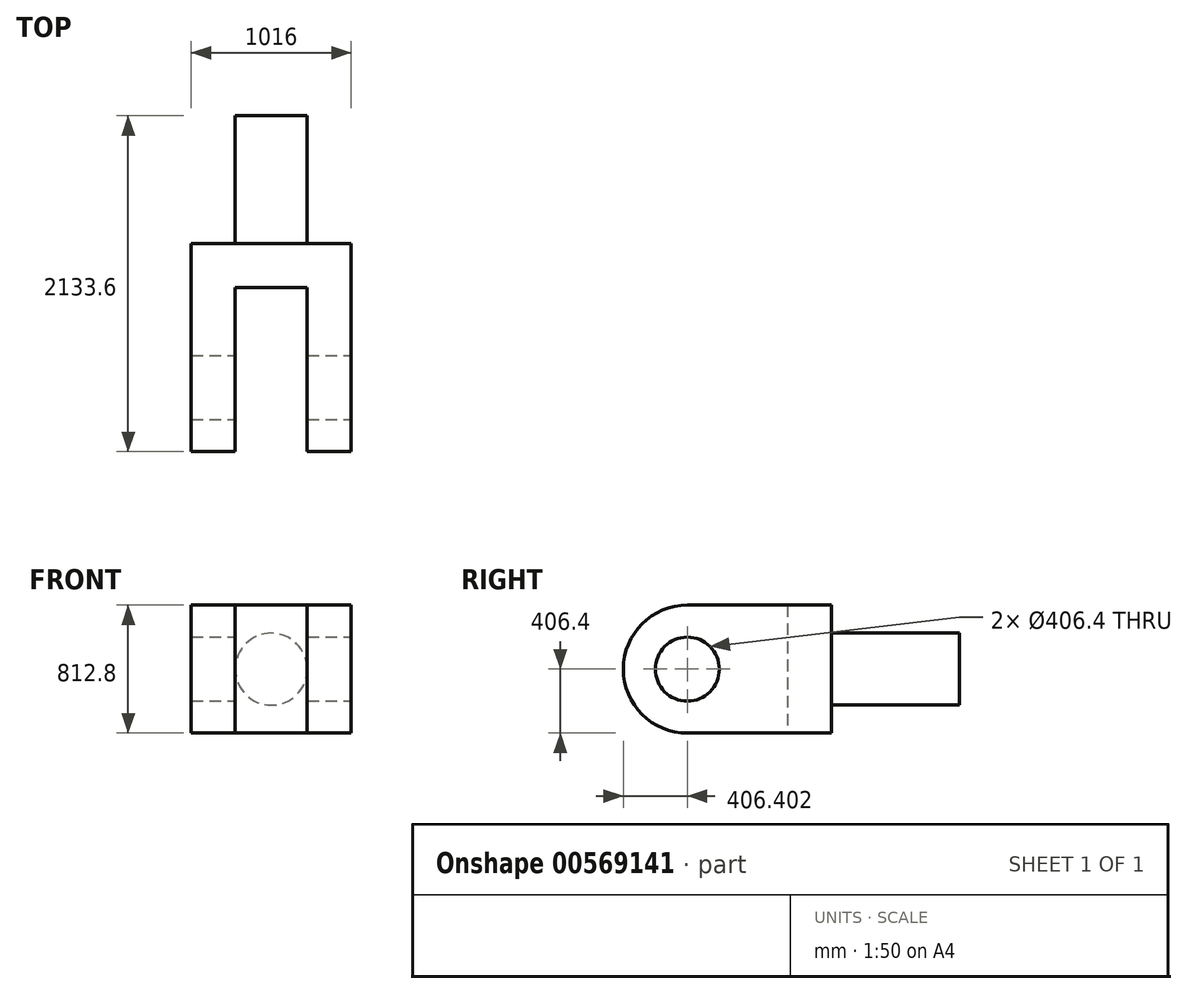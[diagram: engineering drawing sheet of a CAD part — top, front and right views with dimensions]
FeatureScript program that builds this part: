
annotation { "Feature Type Name" : "Feature", "Feature Type Description" : "" }
export const myFeature = defineFeature(function(context is Context, id is Id, definition is map)
    precondition{}
    {
        {
            var Q0;
            Q0=qCreatedBy(makeId("Top.planeOp"),FACE);
            var sketch = newSketch(context, id + "F0", { "sketchPlane" : qUnion([Q0])});
            skLineSegment(sketch, "E0", {"start": v(0, -58.26) * mm, "end": v(279.4, -58.26) * mm});
            skLineSegment(sketch, "E1", {"start": v(279.4, -58.26) * mm, "end": v(279.4, 1262.54) * mm});
            skLineSegment(sketch, "E2", {"start": v(279.4, 1262.54) * mm, "end": v(-736.6, 1262.54) * mm});
            skLineSegment(sketch, "E3", {"start": v(-736.6, 1262.54) * mm, "end": v(-736.6, -58.26) * mm});
            skLineSegment(sketch, "E4", {"start": v(-736.6, -58.26) * mm, "end": v(-457.2, -58.26) * mm});
            skLineSegment(sketch, "E5", {"start": v(-457.2, -58.26) * mm, "end": v(-457.2, 983.14) * mm});
            skLineSegment(sketch, "E6", {"start": v(-457.2, 983.14) * mm, "end": v(0, 983.14) * mm});
            skLineSegment(sketch, "E7", {"start": v(0, 983.14) * mm, "end": v(0, -58.26) * mm});
            skSolve(sketch);
        }
        {
            var Q0;
            Q0=makeQuery(id+"F0.imprint","IMPRINT",FACE,{"disambiguationData":[TD([[makeQuery(id+"F0.imprint","IMPRINT",EDGE,{"derivedFrom":sQuery(id+"F0.wireOp",EDGE,"E0")}),1.0]])]});
            extrude(context, id + "F1", {"entities" : qUnion([Q0]), "depth" : 812.8 * mm, "offsetDistance" : 25.4 * mm});
        }
        {
            var Q0;
            Q0=makeQuery(id+"F1.opExtrude","CAP_FACE",FACE,{"disambiguationData":[OSD([sQuery(id+"F0.wireOp",EDGE,"E0"),sQuery(id+"F0.wireOp",EDGE,"E1"),sQuery(id+"F0.wireOp",EDGE,"E2"),sQuery(id+"F0.wireOp",EDGE,"E3"),sQuery(id+"F0.wireOp",EDGE,"E4"),sQuery(id+"F0.wireOp",EDGE,"E5"),sQuery(id+"F0.wireOp",EDGE,"E6"),sQuery(id+"F0.wireOp",EDGE,"E7")])],"isStart":false});
            var sketch = newSketch(context, id + "F2", { "sketchPlane" : qUnion([Q0])});
            skLineSegment(sketch, "E8", {"start": v(-457.2, 1262.54) * mm, "end": v(-457.2, 2075.34) * mm});
            skLineSegment(sketch, "E9", {"start": v(-457.2, 2075.34) * mm, "end": v(0, 2075.34) * mm});
            skLineSegment(sketch, "E10", {"start": v(0, 2075.34) * mm, "end": v(0, 1262.54) * mm});
            skSolve(sketch);
        }
        {
            var Q0;
            {var subQ0=sQuery(id+"F2.wireOp",EDGE,"E8");Q0=makeQuery(id+"F2.imprint","IMPRINT",FACE,{"disambiguationData":[TD([[makeQuery(id+"F2.imprint","IMPRINT",EDGE,{"derivedFrom":subQ0}),-1.0]])]});}
            extrude(context, id + "F3", {"entities" : qUnion([Q0]), "operationType" : NewBodyOperationType.ADD, "oppositeDirection" : true, "depth" : 812.8 * mm, "offsetDistance" : 25.4 * mm});
        }
        {
            var Q0;
            Q0=makeQuery(id+"F1.opExtrude","CAP_EDGE",EDGE,{"disambiguationData":[OSD([sQuery(id+"F0.wireOp",EDGE,"E0")])],"isStart":false});
            var Q1;
            Q1=makeQuery(id+"F1.opExtrude","CAP_EDGE",EDGE,{"disambiguationData":[OSD([sQuery(id+"F0.wireOp",EDGE,"E4")])],"isStart":false});
            fillet(context, id + "F4", {"entities" : qUnion([Q0, Q1]), "radius" : 406.4 * mm, "tangentPropagation" : true, "allowEdgeOverflow" : false});
        }
        {
            var Q0;
            Q0=makeQuery(id+"F3.opExtrude","SWEPT_FACE",FACE,{"disambiguationData":[OSD([sQuery(id+"F2.wireOp",EDGE,"E9")])]});
            var sketch = newSketch(context, id + "F5", { "sketchPlane" : qUnion([Q0])});
            skCircle(sketch, "E11", {"center": v(228.6, 406.4) * mm, "radius": 228.6 * mm});
            skPoint(sketch, "E11.centerSnap0", {"position": v(457.2, 406.4) * mm});
            skPoint(sketch, "E11.centerSnap1", {"position": v(228.6, 812.8) * mm});
            skSolve(sketch);
        }
        {
            var Q0;
            {var subQ1=sQuery(id+"F2.wireOp",EDGE,"E9");var subQ6=makeQuery(id+"F3.opExtrude","CAP_EDGE",EDGE,{"disambiguationData":[OSD([subQ1])],"isStart":true});Q0=makeQuery(id+"F5.imprint","IMPRINT",FACE,{"disambiguationData":[TD([[makeQuery(id+"F5.imprint","IMPRINT",EDGE,{"derivedFrom":subQ6}),1.0]])]});}
            var Q1;
            {var subQ1=sQuery(id+"F2.wireOp",EDGE,"E9");var subQ6=makeQuery(id+"F3.opExtrude","CAP_EDGE",EDGE,{"disambiguationData":[OSD([subQ1])],"isStart":false});Q1=makeQuery(id+"F5.imprint","IMPRINT",FACE,{"disambiguationData":[TD([[makeQuery(id+"F5.imprint","IMPRINT",EDGE,{"derivedFrom":subQ6}),-1.0]])]});}
            extrude(context, id + "F6", {"entities" : qUnion([Q0, Q1]), "operationType" : NewBodyOperationType.REMOVE, "oppositeDirection" : true, "depth" : 812.8 * mm, "offsetDistance" : 25.4 * mm});
        }
        {
            var Q0;
            Q0=makeQuery(id+"F1.opExtrude","CAP_EDGE",EDGE,{"disambiguationData":[OSD([sQuery(id+"F0.wireOp",EDGE,"E0")])],"isStart":true});
            var Q1;
            Q1=makeQuery(id+"F1.opExtrude","CAP_EDGE",EDGE,{"disambiguationData":[OSD([sQuery(id+"F0.wireOp",EDGE,"E4")])],"isStart":true});
            fillet(context, id + "F7", {"entities" : qUnion([Q0, Q1]), "radius" : 406.4 * mm, "tangentPropagation" : true, "allowEdgeOverflow" : false});
        }
        {
            var Q0;
            Q0=makeQuery(id+"F1.opExtrude","SWEPT_FACE",FACE,{"disambiguationData":[OSD([sQuery(id+"F0.wireOp",EDGE,"E1")])]});
            var sketch = newSketch(context, id + "F8", { "sketchPlane" : qUnion([Q0])});
            skCircle(sketch, "E12", {"center": v(348.14, 406.4) * mm, "radius": 203.2 * mm});
            skSolve(sketch);
        }
        {
            var Q0;
            Q0=makeQuery(id+"F8.imprint","IMPRINT",FACE,{"disambiguationData":[TD([[makeQuery(id+"F8.imprint","IMPRINT",EDGE,{"derivedFrom":sQuery(id+"F8.wireOp",EDGE,"E12")}),1.0]])]});
            extrude(context, id + "F9", {"entities" : qUnion([Q0]), "operationType" : NewBodyOperationType.REMOVE, "endBound" : BoundingType.THROUGH_ALL, "oppositeDirection" : true, "depth" : 25.4 * mm, "offsetDistance" : 25.4 * mm});
        }
    });
